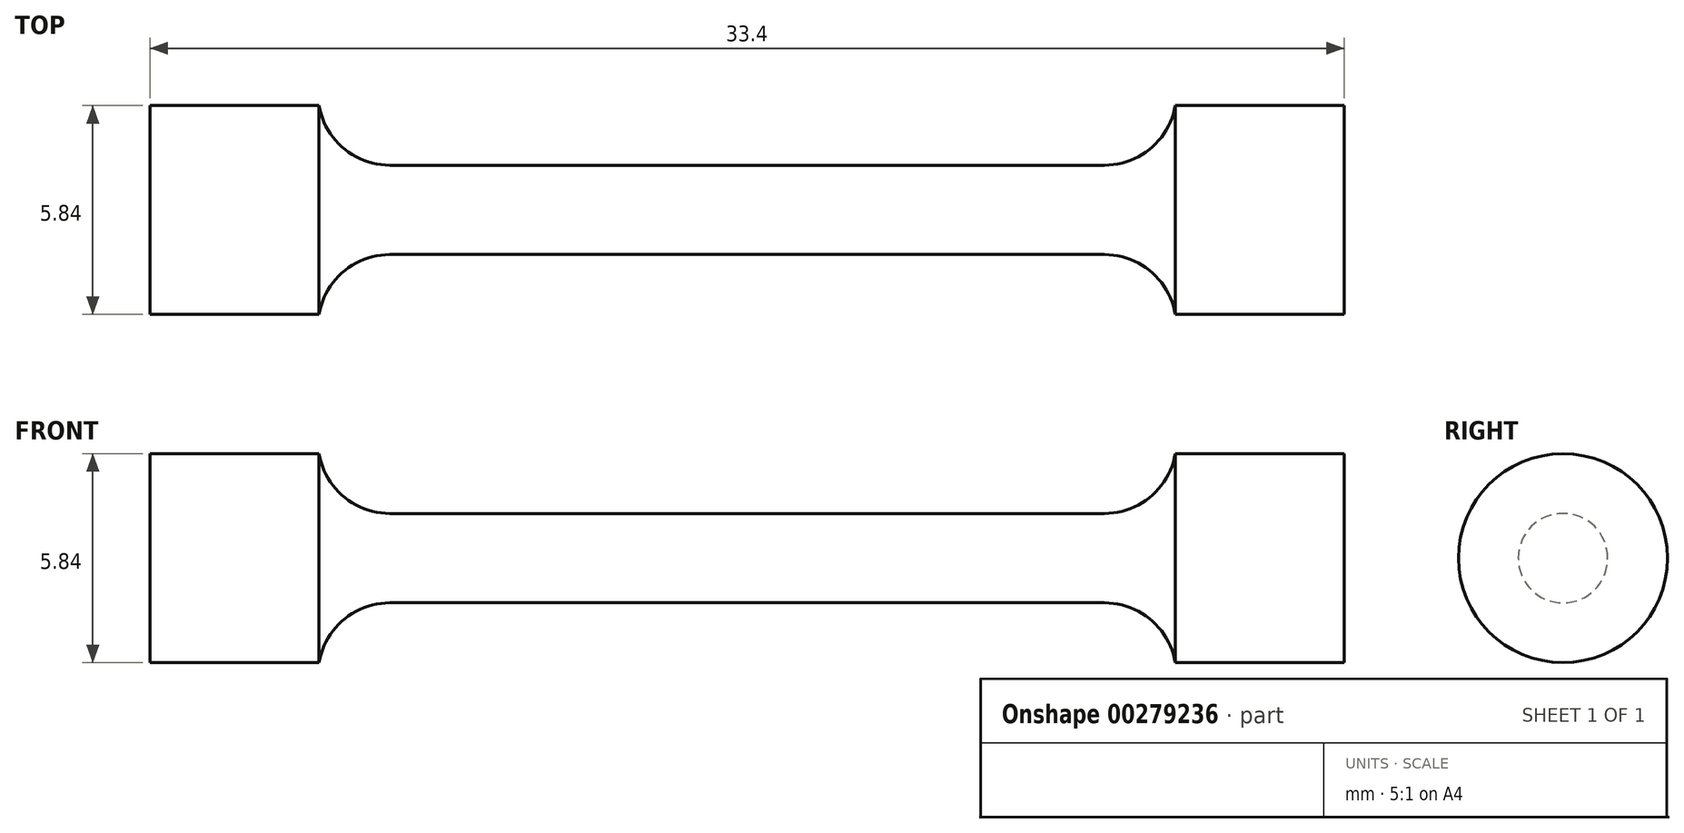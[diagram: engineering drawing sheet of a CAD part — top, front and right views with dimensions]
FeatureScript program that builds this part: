
annotation { "Feature Type Name" : "Feature", "Feature Type Description" : "" }
export const myFeature = defineFeature(function(context is Context, id is Id, definition is map)
    precondition{}
    {
        {
            var Q0;
            Q0=qCreatedBy(makeId("Front.planeOp"),FACE);
            var sketch = newSketch(context, id + "F0", { "sketchPlane" : qUnion([Q0])});
            skLineSegment(sketch, "E0", {"start": v(0, 1.25) * mm, "end": v(10, 1.25) * mm});
            skArc(sketch, "E1", {"start": v(10, 1.25) * mm, "mid": v(11.3, 1.72) * mm, "end": v(11.97, 2.92) * mm});
            skLineSegment(sketch, "E2", {"start": v(11.97, 2.92) * mm, "end": v(16.7, 2.92) * mm});
            skLineSegment(sketch, "E3", {"start": v(16.7, 2.92) * mm, "end": v(16.7, 0) * mm});
            skLineSegment(sketch, "E4.MirrorCS", {"start": v(0, 1.25) * mm, "end": v(-10, 1.25) * mm});
            skLineSegment(sketch, "E5.MirrorCS", {"start": v(-11.97, 2.92) * mm, "end": v(-16.7, 2.92) * mm});
            skLineSegment(sketch, "E6.MirrorCS", {"start": v(-16.7, 2.92) * mm, "end": v(-16.7, 0) * mm});
            skArc(sketch, "E7.MirrorCS", {"start": v(-10, 1.25) * mm, "mid": v(-11.3, 1.72) * mm, "end": v(-11.97, 2.92) * mm});
            skLineSegment(sketch, "E8", {"start": v(-16.7, 0) * mm, "end": v(16.7, 0) * mm});
            skSolve(sketch);
        }
        {
            var Q0;
            Q0=makeQuery(id+"F0.imprint","IMPRINT",FACE,{"disambiguationData":[TD([[makeQuery(id+"F0.imprint","IMPRINT",EDGE,{"derivedFrom":sQuery(id+"F0.wireOp",EDGE,"E0")}),-1.0]])]});
            var Q1;
            Q1=sQuery(id+"F0.wireOp",EDGE,"E8");
            revolve(context, id + "F1", {"entities" : qUnion([Q0]), "axis" : qUnion([Q1]), "revolveType" : RevolveType.FULL});
        }
    });
